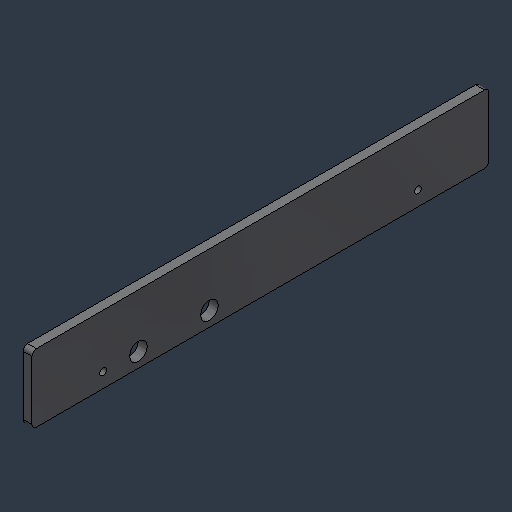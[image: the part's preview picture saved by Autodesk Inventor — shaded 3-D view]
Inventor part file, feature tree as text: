
AUTODESK INVENTOR PART (.ipt)
format: ipt  version: 2024.3 (Build 283343000, 343)  size: 90,112 bytes
history: native  units: mm (DEFAULTED — no unit token found)
features: fillet x1
ambient origin geometry x8: Origin, YZ Plane, XZ Plane, XY Plane, X Axis, Y Axis, Z Axis, Center Point
bodies: Solid1 (feature_tree)
feature tree (1):
  fillet  "Fillet1"  [1 undecoded]
note: 1 required parameter value undecoded (feature->parameter linkage not recoverable at this tier; creation-order binding heuristic only, values carry confidence <= 0.55)
